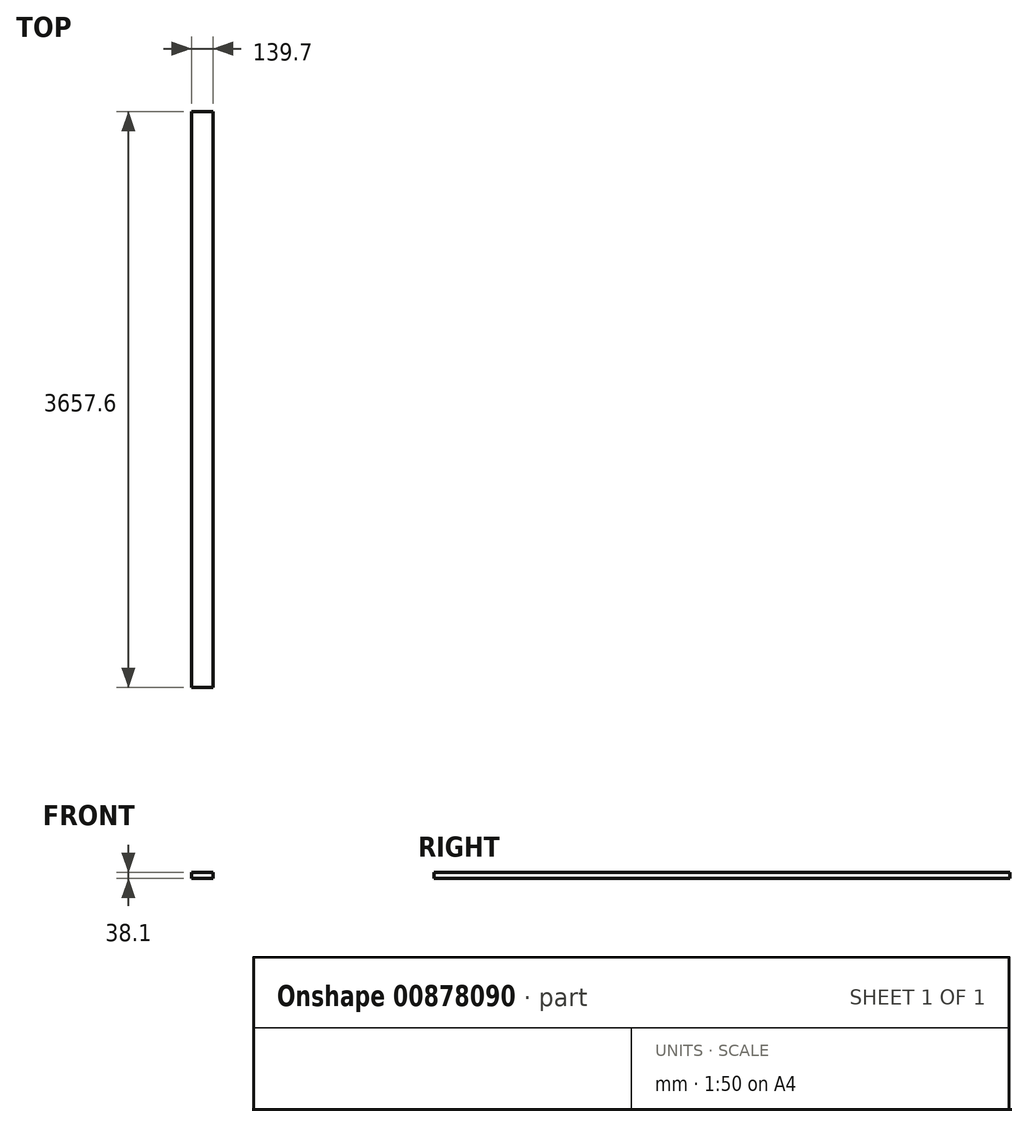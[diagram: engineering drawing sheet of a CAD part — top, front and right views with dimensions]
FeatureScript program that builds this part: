
annotation { "Feature Type Name" : "Feature", "Feature Type Description" : "" }
export const myFeature = defineFeature(function(context is Context, id is Id, definition is map)
    precondition{}
    {
        {
            var Q0;
            Q0=qCreatedBy(makeId("Front.planeOp"),FACE);
            var sketch = newSketch(context, id + "F0", { "sketchPlane" : qUnion([Q0])});
            skLineSegment(sketch, "E0.bottom", {"start": v(69.85, 19.05) * mm, "end": v(-69.85, 19.05) * mm});
            skLineSegment(sketch, "E0.top", {"start": v(69.85, -19.05) * mm, "end": v(-69.85, -19.05) * mm});
            skLineSegment(sketch, "E0.left", {"start": v(69.85, 19.05) * mm, "end": v(69.85, -19.05) * mm});
            skLineSegment(sketch, "E0.right", {"start": v(-69.85, 19.05) * mm, "end": v(-69.85, -19.05) * mm});
            skPoint(sketch, "E0.middle", {"position": v(0, 0) * mm});
            skSolve(sketch);
        }
        {
            var Q0;
            Q0=makeQuery(id+"F0.imprint","IMPRINT",FACE,{"disambiguationData":[TD([[makeQuery(id+"F0.imprint","IMPRINT",EDGE,{"derivedFrom":sQuery(id+"F0.wireOp",EDGE,"E0.bottom")}),1.0]])]});
            extrude(context, id + "F1", {"entities" : qUnion([Q0]), "endBound" : BoundingType.SYMMETRIC, "depth" : 3657.6 * mm, "offsetDistance" : 25.4 * mm});
        }
    });
